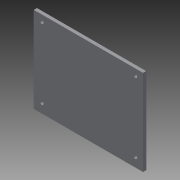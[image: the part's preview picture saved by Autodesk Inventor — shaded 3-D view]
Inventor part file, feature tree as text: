
AUTODESK INVENTOR PART (.ipt)
format: ipt  version: 2014 (Build 180170000, 170)  size: 74,240 bytes
history: native  units: mm
features: plane x1, extrude x1, sketch x1
ambient origin geometry x8: Origin, YZ Plane, XZ Plane, XY Plane, X Axis, Y Axis, Z Axis, Center Point
bodies: Body1 (feature_tree)
feature tree (3):
  plane  "Work Plane1"
  extrude  "Extrusion3"  [1 undecoded]
  sketch  "Sketch2"  dims[d7=4.0mm d8=0.0mm]
note: 1 required parameter value undecoded (feature->parameter linkage not recoverable at this tier; creation-order binding heuristic only, values carry confidence <= 0.55)
